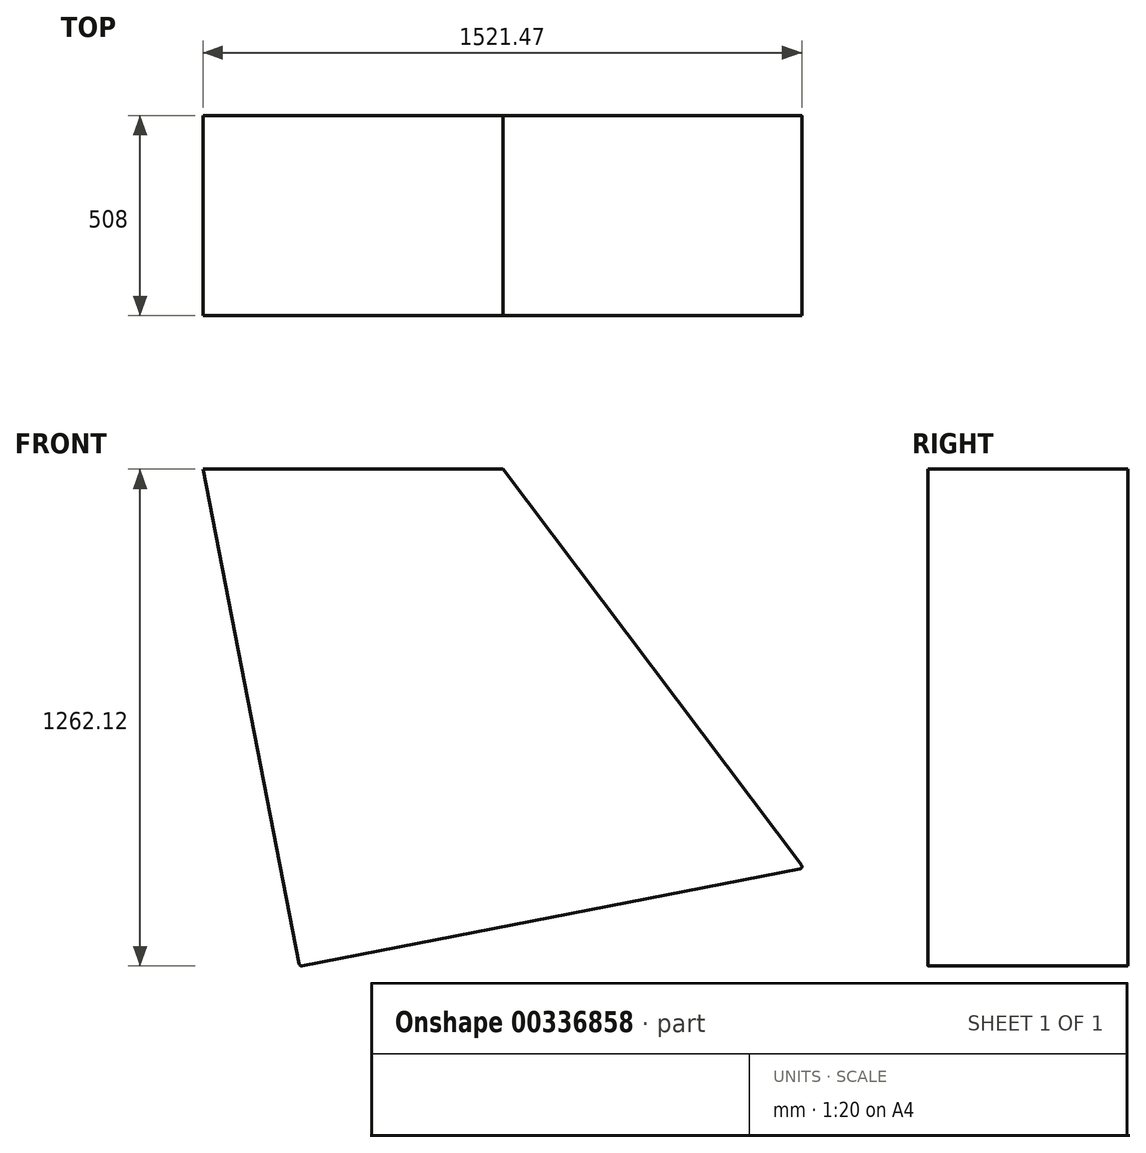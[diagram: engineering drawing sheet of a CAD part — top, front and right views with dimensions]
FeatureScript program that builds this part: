
annotation { "Feature Type Name" : "Feature", "Feature Type Description" : "" }
export const myFeature = defineFeature(function(context is Context, id is Id, definition is map)
    precondition{}
    {
        {
            var Q0;
            Q0=qCreatedBy(makeId("Front.planeOp"),FACE);
            var sketch = newSketch(context, id + "F0", { "sketchPlane" : qUnion([Q0])});
            skLineSegment(sketch, "E0", {"start": v(-514.68, -849) * mm, "end": v(763.53, -600.54) * mm});
            skLineSegment(sketch, "E1", {"start": v(767.39, -590.49) * mm, "end": v(9.2, 415.66) * mm});
            skLineSegment(sketch, "E2", {"start": v(9.2, 415.66) * mm, "end": v(-752.8, 415.66) * mm});
            skLineSegment(sketch, "E3", {"start": v(-752.8, 415.66) * mm, "end": v(-508.47, -841.33) * mm});
            skArc(sketch, "E4.filletArc", {"start": v(-508.47, -841.33) * mm, "mid": v(-505.79, -845.38) * mm, "end": v(-501.02, -846.35) * mm});
            skPoint(sketch, "E5.visualSharp", {"position": v(773.5, -598.6) * mm});
            skArc(sketch, "E5.filletArc", {"start": v(763.53, -600.54) * mm, "mid": v(768.24, -596.59) * mm, "end": v(767.39, -590.49) * mm});
            skSolve(sketch);
        }
        {
            var Q0;
            Q0=makeQuery(id+"F0.imprint","IMPRINT",FACE,{"disambiguationData":[TD([[makeQuery(id+"F0.imprint","IMPRINT",EDGE,{"derivedFrom":sQuery(id+"F0.wireOp",EDGE,"E1")}),1.0]])]});
            extrude(context, id + "F1", {"entities" : qUnion([Q0]), "depth" : 508 * mm});
        }
    });
